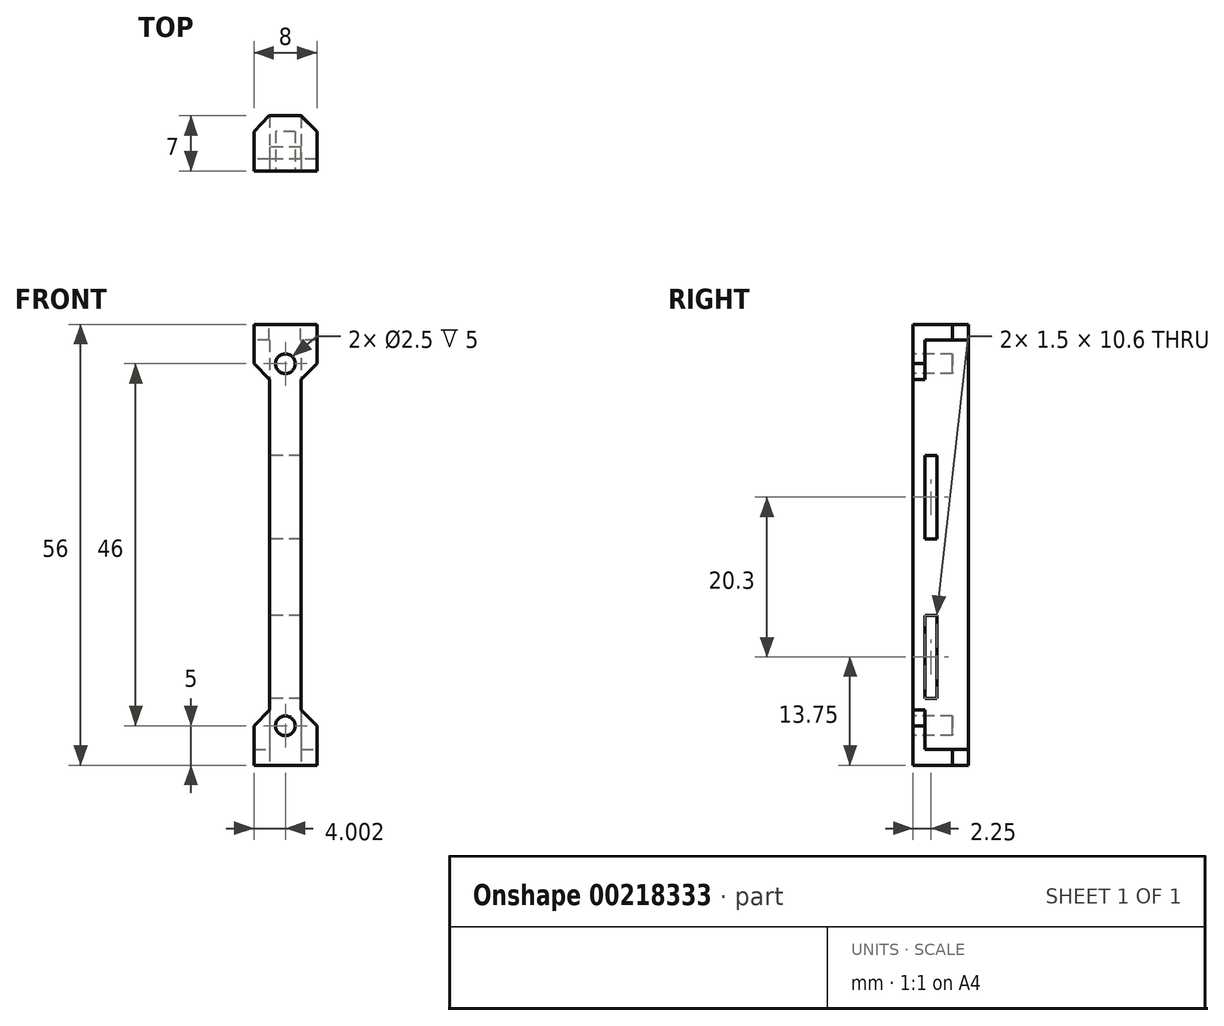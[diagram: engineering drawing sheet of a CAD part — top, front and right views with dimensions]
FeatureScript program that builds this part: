
annotation { "Feature Type Name" : "Feature", "Feature Type Description" : "" }
export const myFeature = defineFeature(function(context is Context, id is Id, definition is map)
    precondition{}
    {
        {
            var Q0;
            Q0=qCreatedBy(makeId("Top.planeOp"),FACE);
            var sketch = newSketch(context, id + "F0", { "sketchPlane" : qUnion([Q0])});
            skLineSegment(sketch, "E0", {"start": v(-32.85, 6.78) * mm, "end": v(-24.85, 6.78) * mm});
            skLineSegment(sketch, "E1", {"start": v(-32.85, 6.78) * mm, "end": v(-32.85, 11.78) * mm});
            skLineSegment(sketch, "E2", {"start": v(-32.85, 11.78) * mm, "end": v(-30.85, 13.78) * mm});
            skLineSegment(sketch, "E3", {"start": v(-30.85, 13.78) * mm, "end": v(-26.85, 13.78) * mm});
            skLineSegment(sketch, "E4", {"start": v(-26.85, 13.78) * mm, "end": v(-24.85, 11.78) * mm});
            skLineSegment(sketch, "E5", {"start": v(-24.85, 11.78) * mm, "end": v(-24.85, 6.78) * mm});
            skLineSegment(sketch, "E6", {"start": v(-28.85, 13.78) * mm, "end": v(-28.85, 6.78) * mm, "construction": true});
            skSolve(sketch);
        }
        {
            var Q0;
            Q0=makeQuery(id+"F0.imprint","IMPRINT",FACE,{"disambiguationData":[TD([[makeQuery(id+"F0.imprint","IMPRINT",EDGE,{"derivedFrom":sQuery(id+"F0.wireOp",EDGE,"E0")}),1.0]])]});
            extrude(context, id + "F1", {"entities" : qUnion([Q0]), "depth" : 2 * mm});
        }
        {
            var Q0;
            Q0=makeQuery(id+"F1.opExtrude","SWEPT_FACE",FACE,{"disambiguationData":[OSD([sQuery(id+"F0.wireOp",EDGE,"E0")])]});
            var sketch = newSketch(context, id + "F2", { "sketchPlane" : qUnion([Q0])});
            skLineSegment(sketch, "E7", {"start": v(-32.85, 2) * mm, "end": v(-32.85, 5) * mm});
            skLineSegment(sketch, "E8", {"start": v(-24.85, 2) * mm, "end": v(-24.85, 5) * mm});
            skLineSegment(sketch, "E9", {"start": v(-32.85, 5) * mm, "end": v(-30.85, 7) * mm});
            skLineSegment(sketch, "E10", {"start": v(-24.85, 5) * mm, "end": v(-26.85, 7) * mm});
            skLineSegment(sketch, "E11", {"start": v(-26.85, 7) * mm, "end": v(-26.85, 49) * mm});
            skLineSegment(sketch, "E12", {"start": v(-26.85, 49) * mm, "end": v(-24.85, 51) * mm});
            skLineSegment(sketch, "E13", {"start": v(-24.85, 51) * mm, "end": v(-24.85, 56) * mm});
            skLineSegment(sketch, "E14", {"start": v(-24.85, 56) * mm, "end": v(-32.85, 56) * mm});
            skLineSegment(sketch, "E15", {"start": v(-32.85, 56) * mm, "end": v(-32.85, 51) * mm});
            skLineSegment(sketch, "E16", {"start": v(-32.85, 51) * mm, "end": v(-30.85, 49) * mm});
            skLineSegment(sketch, "E17", {"start": v(-30.85, 49) * mm, "end": v(-30.85, 7) * mm});
            skLineSegment(sketch, "E18", {"start": v(-32.85, 2) * mm, "end": v(-24.85, 2) * mm});
            skLineSegment(sketch, "E19", {"start": v(-28.85, 2) * mm, "end": v(-28.85, 56) * mm, "construction": true});
            skSolve(sketch);
        }
        {
            var Q0;
            Q0=makeQuery(id+"F2.imprint","IMPRINT",FACE,{"disambiguationData":[TD([[makeQuery(id+"F2.imprint","IMPRINT",EDGE,{"derivedFrom":sQuery(id+"F2.wireOp",EDGE,"E7")}),-1.0]])]});
            extrude(context, id + "F3", {"entities" : qUnion([Q0]), "operationType" : NewBodyOperationType.ADD, "oppositeDirection" : true, "depth" : 1.5 * mm});
        }
        {
            var Q0;
            Q0=makeQuery(id+"F3.boolean.opBoolean","MERGE",FACE,{"derivedFrom":[makeQuery(id+"F1.opExtrude","SWEPT_FACE",FACE,{"disambiguationData":[OSD([sQuery(id+"F0.wireOp",EDGE,"E0")])]}),makeQuery(id+"F3.opExtrude","CAP_FACE",FACE,{"disambiguationData":[OSD([sQuery(id+"F2.wireOp",EDGE,"E7"),sQuery(id+"F2.wireOp",EDGE,"E8"),sQuery(id+"F2.wireOp",EDGE,"E9"),sQuery(id+"F2.wireOp",EDGE,"E10"),sQuery(id+"F2.wireOp",EDGE,"E11"),sQuery(id+"F2.wireOp",EDGE,"E12"),sQuery(id+"F2.wireOp",EDGE,"E13"),sQuery(id+"F2.wireOp",EDGE,"E14"),sQuery(id+"F2.wireOp",EDGE,"E15"),sQuery(id+"F2.wireOp",EDGE,"E16"),sQuery(id+"F2.wireOp",EDGE,"E17"),sQuery(id+"F2.wireOp",EDGE,"E18")])],"isStart":true})]});
            var sketch = newSketch(context, id + "F4", { "sketchPlane" : qUnion([Q0])});
            skLineSegment(sketch, "E20", {"start": v(-28.85, 0) * mm, "end": v(-28.85, 5) * mm, "construction": true});
            skCircle(sketch, "E21", {"center": v(-28.85, 5) * mm, "radius": 1.25 * mm});
            skLineSegment(sketch, "E22", {"start": v(-28.85, 56) * mm, "end": v(-28.85, 51) * mm, "construction": true});
            skCircle(sketch, "E23", {"center": v(-28.85, 51) * mm, "radius": 1.25 * mm});
            skSolve(sketch);
        }
        {
            var Q0;
            Q0=makeQuery(id+"F1.opExtrude","CAP_FACE",FACE,{"disambiguationData":[OSD([sQuery(id+"F0.wireOp",EDGE,"E0"),sQuery(id+"F0.wireOp",EDGE,"E1"),sQuery(id+"F0.wireOp",EDGE,"E2"),sQuery(id+"F0.wireOp",EDGE,"E3"),sQuery(id+"F0.wireOp",EDGE,"E4"),sQuery(id+"F0.wireOp",EDGE,"E5")])],"isStart":false});
            var sketch = newSketch(context, id + "F5", { "sketchPlane" : qUnion([Q0])});
            skLineSegment(sketch, "E24", {"start": v(-26.85, 13.78) * mm, "end": v(-26.85, 8.28) * mm});
            skLineSegment(sketch, "E25", {"start": v(-30.85, 13.78) * mm, "end": v(-30.85, 8.28) * mm});
            skLineSegment(sketch, "E26", {"start": v(-26.85, 13.78) * mm, "end": v(-30.85, 13.78) * mm});
            skLineSegment(sketch, "E27", {"start": v(-30.85, 8.28) * mm, "end": v(-26.85, 8.28) * mm});
            skSolve(sketch);
        }
        {
            var Q0;
            Q0=makeQuery(id+"F5.imprint","IMPRINT",FACE,{"disambiguationData":[TD([[makeQuery(id+"F5.imprint","IMPRINT",EDGE,{"derivedFrom":sQuery(id+"F5.wireOp",EDGE,"E24")}),-1.0]])]});
            extrude(context, id + "F6", {"entities" : qUnion([Q0]), "operationType" : NewBodyOperationType.ADD, "depth" : (62 - 6 - 4) * mm});
        }
        {
            var Q0;
            Q0 = qSketchRegion(id + "F4", true);
            extrude(context, id + "F7", {"entities" : qUnion([Q0]), "operationType" : NewBodyOperationType.REMOVE, "oppositeDirection" : true, "depth" : 5 * mm});
        }
        {
            var Q0;
            Q0=makeQuery(id+"F6.opExtrude","SWEPT_FACE",FACE,{"disambiguationData":[OSD([sQuery(id+"F5.wireOp",EDGE,"E25")])]});
            var sketch = newSketch(context, id + "F8", { "sketchPlane" : qUnion([Q0])});
            skLineSegment(sketch, "E28", {"start": v(-8.28, 5.8) * mm, "end": v(-9.78, 5.8) * mm, "construction": true});
            skLineSegment(sketch, "E29", {"start": v(-9.78, 5.8) * mm, "end": v(-9.78, 42) * mm, "construction": true});
            skLineSegment(sketch, "E30", {"start": v(-9.78, 42) * mm, "end": v(-8.28, 42) * mm, "construction": true});
            skLineSegment(sketch, "E31.bottom", {"start": v(-9.78, 8.45) * mm, "end": v(-8.28, 8.45) * mm});
            skLineSegment(sketch, "E31.top", {"start": v(-9.78, 19.05) * mm, "end": v(-8.28, 19.05) * mm});
            skLineSegment(sketch, "E31.left", {"start": v(-9.78, 8.45) * mm, "end": v(-9.78, 19.05) * mm});
            skLineSegment(sketch, "E31.right", {"start": v(-8.28, 8.45) * mm, "end": v(-8.28, 19.05) * mm});
            skLineSegment(sketch, "E32.bottom", {"start": v(-9.78, 39.35) * mm, "end": v(-8.28, 39.35) * mm});
            skLineSegment(sketch, "E32.top", {"start": v(-9.78, 28.75) * mm, "end": v(-8.28, 28.75) * mm});
            skLineSegment(sketch, "E32.left", {"start": v(-9.78, 39.35) * mm, "end": v(-9.78, 28.75) * mm});
            skLineSegment(sketch, "E32.right", {"start": v(-8.28, 39.35) * mm, "end": v(-8.28, 28.75) * mm});
            skSolve(sketch);
        }
        {
            var Q0;
            Q0 = qSketchRegion(id + "F8", true);
            extrude(context, id + "F9", {"entities" : qUnion([Q0]), "operationType" : NewBodyOperationType.REMOVE, "oppositeDirection" : true, "depth" : 25 * mm});
        }
        {
            var Q0;
            Q0=makeQuery(id+"F3.opExtrude","SWEPT_FACE",FACE,{"disambiguationData":[OSD([sQuery(id+"F2.wireOp",EDGE,"E14")])]});
            var sketch = newSketch(context, id + "F10", { "sketchPlane" : qUnion([Q0])});
            skLineSegment(sketch, "E33", {"start": v(-24.85, 8.28) * mm, "end": v(-24.85, 11.78) * mm});
            skLineSegment(sketch, "E34", {"start": v(-24.85, 11.78) * mm, "end": v(-26.9, 13.78) * mm});
            skLineSegment(sketch, "E35", {"start": v(-26.9, 13.78) * mm, "end": v(-30.9, 13.78) * mm});
            skLineSegment(sketch, "E36", {"start": v(-30.9, 13.78) * mm, "end": v(-32.85, 11.78) * mm});
            skLineSegment(sketch, "E37", {"start": v(-32.85, 11.78) * mm, "end": v(-32.85, 8.28) * mm});
            skLineSegment(sketch, "E38", {"start": v(-32.85, 8.28) * mm, "end": v(-24.85, 8.28) * mm});
            skSolve(sketch);
        }
        {
            var Q0;
            Q0=makeQuery(id+"F10.imprint","IMPRINT",FACE,{"disambiguationData":[TD([[makeQuery(id+"F10.imprint","IMPRINT",EDGE,{"derivedFrom":sQuery(id+"F10.wireOp",EDGE,"E33")}),1.0]])]});
            extrude(context, id + "F11", {"entities" : qUnion([Q0]), "operationType" : NewBodyOperationType.ADD, "oppositeDirection" : true, "depth" : 2 * mm});
        }
    });
